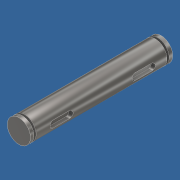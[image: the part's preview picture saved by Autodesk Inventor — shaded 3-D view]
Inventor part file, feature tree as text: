
AUTODESK INVENTOR PART (.ipt)
format: ipt  version: 2018 (Build 220112000, 112)  size: 162,304 bytes
history: native  units: mm
features: extrude x3, sketch x2, revolve x1, plane x1, projected_geometry x1
ambient origin geometry x8: Origin, YZ Plane, XZ Plane, XY Plane, X Axis, Y Axis, Z Axis, Center Point
bodies: Solid1 (feature_tree)
feature tree (8):
  extrude  "Extrusion1"  Depth=10.0mm TaperAngle=0.0deg
  extrude  "Extrusion2"  Depth=3.0mm
  revolve  "Revolution1"  [1 undecoded]
  plane  "Work Plane1"
  extrude  "Extrusion4"  Depth=1.5mm
  sketch  "Sketch2"  dims[d0=10.0mm d1=3.6mm d2=58.3mm d3=0.0mm]
  projected_geometry  "Projected Loop1"
  sketch  "Sketch6"  dims[d7=3.0mm d8=0.0mm d10=0.94mm d11=4.0mm d12=1.5mm d13=90.0deg d21=1.5mm d22=3.0mm d23=3.5mm d24=7.0mm d25=7.0mm d26=3.0mm d27=3.5mm d30=1.8mm d31=0.0mm d33=7.5mm d34=6.5mm]
note: 1 required parameter value undecoded (feature->parameter linkage not recoverable at this tier; creation-order binding heuristic only, values carry confidence <= 0.55)
